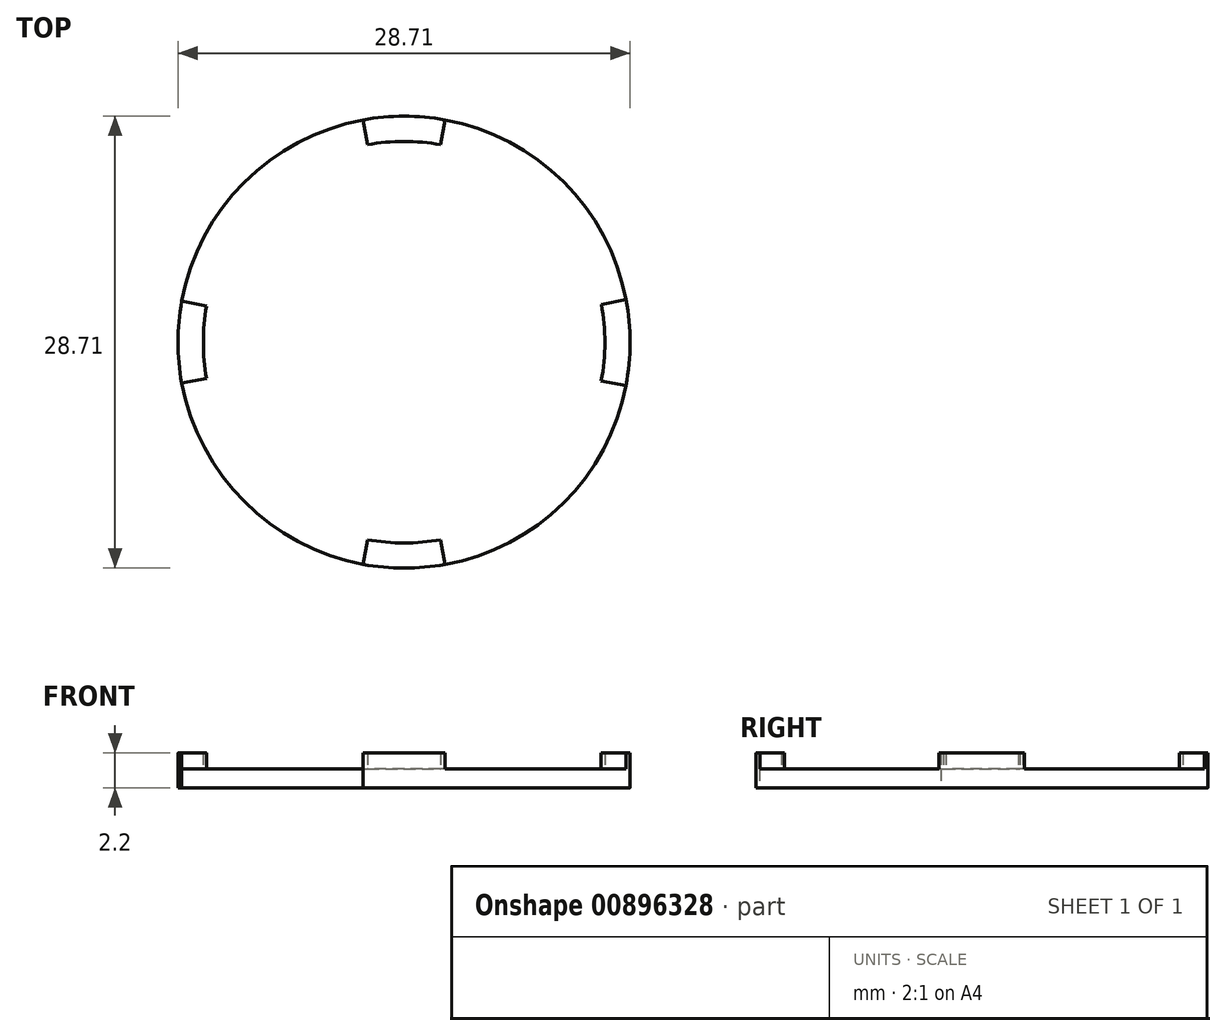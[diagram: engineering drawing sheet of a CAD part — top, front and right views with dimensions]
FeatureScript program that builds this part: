
annotation { "Feature Type Name" : "Feature", "Feature Type Description" : "" }
export const myFeature = defineFeature(function(context is Context, id is Id, definition is map)
    precondition{}
    {
        {
            var Q0;
            Q0=qCreatedBy(makeId("Top.planeOp"),FACE);
            var sketch = newSketch(context, id + "F0", { "sketchPlane" : qUnion([Q0])});
            skArc(sketch, "E0", {"start": v(-14.12, 2.6) * mm, "mid": v(-14.35, 0) * mm, "end": v(-14.12, -2.6) * mm});
            skArc(sketch, "E1", {"start": v(-2.61, -14.12) * mm, "mid": v(0, -14.35) * mm, "end": v(2.62, -14.12) * mm});
            skArc(sketch, "E2", {"start": v(14.1, -2.75) * mm, "mid": v(14.36, -0.03) * mm, "end": v(14.1, 2.7) * mm});
            skArc(sketch, "E3", {"start": v(2.61, 14.12) * mm, "mid": v(0, 14.36) * mm, "end": v(-2.61, 14.12) * mm});
            skLineSegment(sketch, "E4", {"start": v(-2.61, 14.12) * mm, "end": v(-2.32, 12.55) * mm});
            skLineSegment(sketch, "E5", {"start": v(2.61, 14.12) * mm, "end": v(2.32, 12.55) * mm});
            skLineSegment(sketch, "E6", {"start": v(-14.12, 2.6) * mm, "end": v(-12.55, 2.3) * mm});
            skLineSegment(sketch, "E7", {"start": v(-14.12, -2.6) * mm, "end": v(-12.55, -2.3) * mm});
            skLineSegment(sketch, "E8", {"start": v(-2.61, -14.12) * mm, "end": v(-2.32, -12.55) * mm});
            skLineSegment(sketch, "E9", {"start": v(14.1, 2.7) * mm, "end": v(12.53, 2.4) * mm});
            skLineSegment(sketch, "E10", {"start": v(14.1, -2.75) * mm, "end": v(12.52, -2.45) * mm});
            skLineSegment(sketch, "E11", {"start": v(2.62, -14.12) * mm, "end": v(2.32, -12.55) * mm});
            skArc(sketch, "E12", {"start": v(-14.12, -2.6) * mm, "mid": v(-10.14, -10.13) * mm, "end": v(-2.61, -14.12) * mm});
            skArc(sketch, "E13", {"start": v(2.62, -14.12) * mm, "mid": v(10.12, -10.22) * mm, "end": v(14.1, -2.75) * mm});
            skArc(sketch, "E14", {"start": v(14.1, 2.7) * mm, "mid": v(10.13, 10.2) * mm, "end": v(2.61, 14.12) * mm});
            skArc(sketch, "E15", {"start": v(-2.61, 14.12) * mm, "mid": v(-10.15, 10.15) * mm, "end": v(-14.12, 2.6) * mm});
            skArc(sketch, "E16", {"start": v(2.32, 12.55) * mm, "mid": v(0, 12.75) * mm, "end": v(-2.32, 12.55) * mm});
            skArc(sketch, "E17", {"start": v(-12.55, 2.3) * mm, "mid": v(-12.75, 0) * mm, "end": v(-12.55, -2.3) * mm});
            skArc(sketch, "E18", {"start": v(-2.32, -12.55) * mm, "mid": v(0, -12.75) * mm, "end": v(2.32, -12.55) * mm});
            skArc(sketch, "E19", {"start": v(12.52, -2.45) * mm, "mid": v(12.76, -0.02) * mm, "end": v(12.53, 2.4) * mm});
            skSolve(sketch);
        }
        {
            var Q0;
            Q0=makeQuery(id+"F0.imprint","IMPRINT",FACE,{"disambiguationData":[TD([[makeQuery(id+"F0.imprint","IMPRINT",EDGE,{"derivedFrom":sQuery(id+"F0.wireOp",EDGE,"E4")}),-1.0]])]});
            extrude(context, id + "F1", {"entities" : qUnion([Q0]), "depth" : 1.2 * mm, "offsetDistance" : 25 * mm});
        }
        {
            var Q0;
            Q0=makeQuery(id+"F0.imprint","IMPRINT",FACE,{"disambiguationData":[TD([[makeQuery(id+"F0.imprint","IMPRINT",EDGE,{"derivedFrom":sQuery(id+"F0.wireOp",EDGE,"E0")}),1.0]])]});
            var Q1;
            Q1=makeQuery(id+"F0.imprint","IMPRINT",FACE,{"disambiguationData":[TD([[makeQuery(id+"F0.imprint","IMPRINT",EDGE,{"derivedFrom":sQuery(id+"F0.wireOp",EDGE,"E3")}),1.0]])]});
            var Q2;
            Q2=makeQuery(id+"F0.imprint","IMPRINT",FACE,{"disambiguationData":[TD([[makeQuery(id+"F0.imprint","IMPRINT",EDGE,{"derivedFrom":sQuery(id+"F0.wireOp",EDGE,"E2")}),1.0]])]});
            var Q3;
            Q3=makeQuery(id+"F0.imprint","IMPRINT",FACE,{"disambiguationData":[TD([[makeQuery(id+"F0.imprint","IMPRINT",EDGE,{"derivedFrom":sQuery(id+"F0.wireOp",EDGE,"E1")}),1.0]])]});
            extrude(context, id + "F2", {"entities" : qUnion([Q0, Q1, Q2, Q3]), "operationType" : NewBodyOperationType.ADD, "depth" : 2.2 * mm, "offsetDistance" : 25 * mm});
        }
    });
